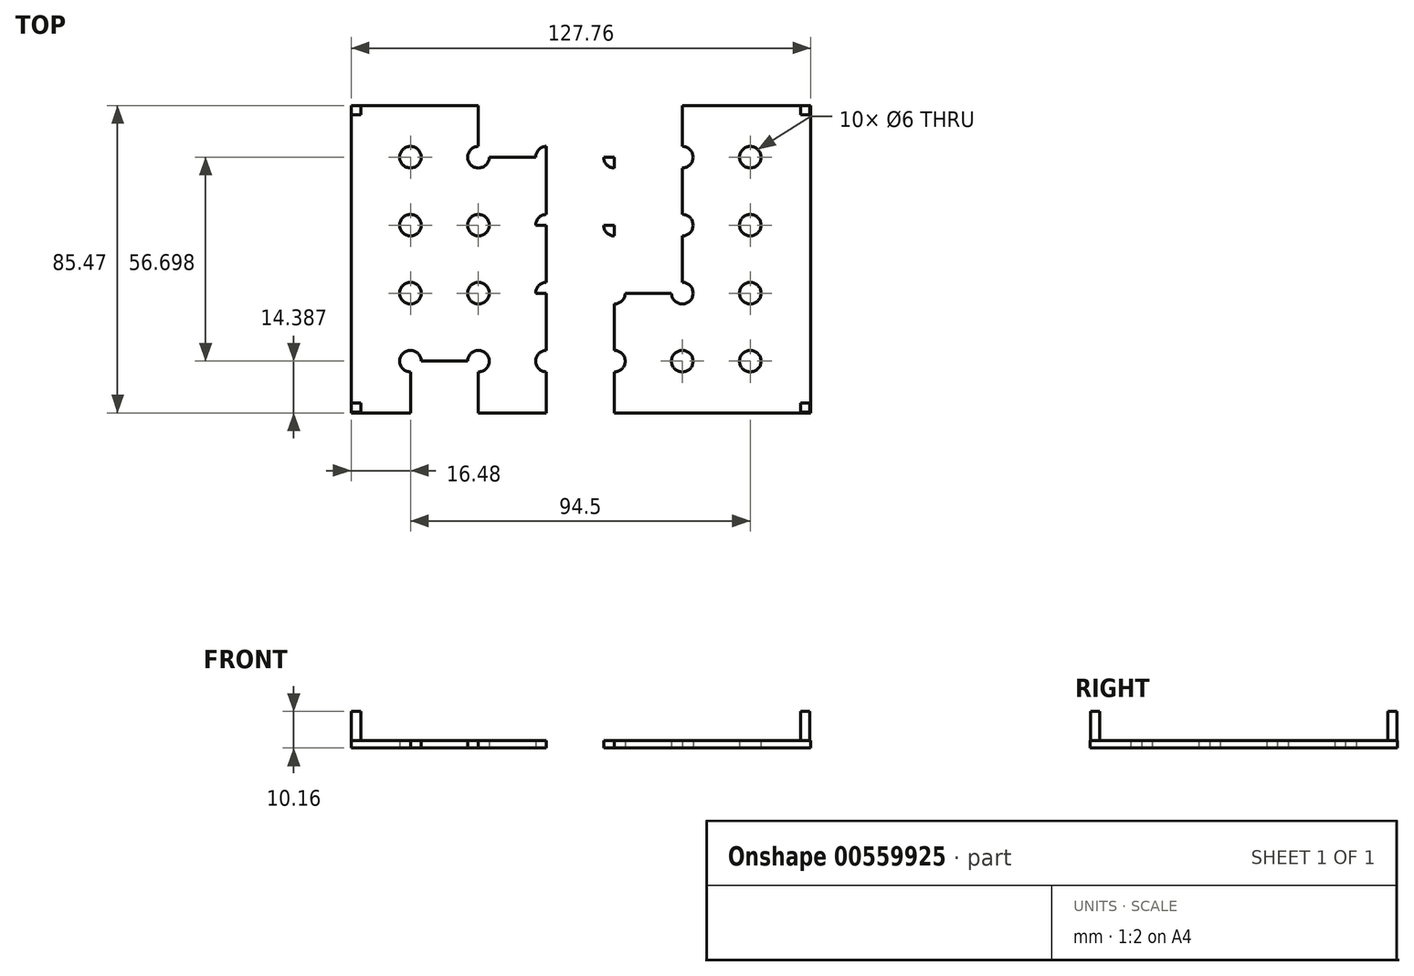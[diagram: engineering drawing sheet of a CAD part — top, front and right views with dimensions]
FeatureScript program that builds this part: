
annotation { "Feature Type Name" : "Feature", "Feature Type Description" : "" }
export const myFeature = defineFeature(function(context is Context, id is Id, definition is map)
    precondition{}
    {
        {
            var Q0;
            Q0=qCreatedBy(makeId("Top.planeOp"),FACE);
            var sketch = newSketch(context, id + "F0", { "sketchPlane" : qUnion([Q0])});
            skLineSegment(sketch, "E0.bottom", {"start": v(63.88, 42.74) * mm, "end": v(-63.88, 42.74) * mm});
            skLineSegment(sketch, "E0.top", {"start": v(63.88, -42.73) * mm, "end": v(-63.88, -42.73) * mm});
            skLineSegment(sketch, "E0.left", {"start": v(63.88, 42.74) * mm, "end": v(63.88, -42.73) * mm});
            skLineSegment(sketch, "E0.right", {"start": v(-63.88, 42.74) * mm, "end": v(-63.88, -42.73) * mm});
            skPoint(sketch, "E0.middle", {"position": v(0, 0) * mm});
            skLineSegment(sketch, "E1", {"start": v(-63.88, 28.34) * mm, "end": v(63.88, 28.35) * mm});
            skLineSegment(sketch, "E2", {"start": v(-63.88, 9.44) * mm, "end": v(63.88, 9.45) * mm});
            skLineSegment(sketch, "E3", {"start": v(-63.88, -9.45) * mm, "end": v(63.88, -9.45) * mm});
            skLineSegment(sketch, "E4", {"start": v(-47.4, 42.74) * mm, "end": v(-47.4, -42.73) * mm});
            skLineSegment(sketch, "E5", {"start": v(-47.4, -42.74) * mm, "end": v(-28.5, -42.73) * mm});
            skLineSegment(sketch, "E6", {"start": v(-28.5, -42.73) * mm, "end": v(-28.5, 42.74) * mm});
            skLineSegment(sketch, "E7", {"start": v(-28.5, 42.74) * mm, "end": v(-9.6, 42.74) * mm});
            skLineSegment(sketch, "E8", {"start": v(-9.6, 42.74) * mm, "end": v(-9.6, -42.73) * mm});
            skLineSegment(sketch, "E9", {"start": v(-9.6, -42.74) * mm, "end": v(9.3, -42.73) * mm});
            skLineSegment(sketch, "E10", {"start": v(9.3, -42.73) * mm, "end": v(9.3, 42.74) * mm});
            skLineSegment(sketch, "E11", {"start": v(9.3, 42.74) * mm, "end": v(28.2, 42.74) * mm});
            skLineSegment(sketch, "E12", {"start": v(28.2, 42.74) * mm, "end": v(28.2, -42.73) * mm});
            skLineSegment(sketch, "E13", {"start": v(47.1, 42.74) * mm, "end": v(47.1, -42.73) * mm});
            skLineSegment(sketch, "E14", {"start": v(-63.88, -28.35) * mm, "end": v(63.88, -28.35) * mm});
            skCircle(sketch, "E15", {"center": v(-47.4, 28.34) * mm, "radius": 3 * mm});
            skCircle(sketch, "E16", {"center": v(-47.4, 9.45) * mm, "radius": 3 * mm});
            skCircle(sketch, "E17", {"center": v(-47.4, -9.46) * mm, "radius": 3 * mm});
            skCircle(sketch, "E18", {"center": v(-47.4, -28.35) * mm, "radius": 3 * mm});
            skCircle(sketch, "E19", {"center": v(-28.5, 28.34) * mm, "radius": 3 * mm});
            skCircle(sketch, "E20", {"center": v(-28.5, 9.45) * mm, "radius": 3 * mm});
            skCircle(sketch, "E21", {"center": v(-28.5, -9.46) * mm, "radius": 3 * mm});
            skCircle(sketch, "E22", {"center": v(-28.5, -28.35) * mm, "radius": 3 * mm});
            skCircle(sketch, "E23", {"center": v(-9.6, 28.34) * mm, "radius": 3 * mm});
            skCircle(sketch, "E24", {"center": v(-9.6, 9.45) * mm, "radius": 3 * mm});
            skCircle(sketch, "E25", {"center": v(-9.6, -9.46) * mm, "radius": 3 * mm});
            skCircle(sketch, "E26", {"center": v(-9.6, -28.35) * mm, "radius": 3 * mm});
            skCircle(sketch, "E27", {"center": v(9.3, 28.34) * mm, "radius": 3 * mm});
            skCircle(sketch, "E28", {"center": v(9.3, 9.45) * mm, "radius": 3 * mm});
            skCircle(sketch, "E29", {"center": v(9.3, -9.46) * mm, "radius": 3 * mm});
            skCircle(sketch, "E30", {"center": v(9.3, -28.35) * mm, "radius": 3 * mm});
            skCircle(sketch, "E31", {"center": v(28.2, 28.34) * mm, "radius": 3 * mm});
            skCircle(sketch, "E32", {"center": v(28.2, 9.45) * mm, "radius": 3 * mm});
            skCircle(sketch, "E33", {"center": v(28.2, -9.46) * mm, "radius": 3 * mm});
            skCircle(sketch, "E34", {"center": v(28.2, -28.35) * mm, "radius": 3 * mm});
            skCircle(sketch, "E35", {"center": v(47.1, 28.34) * mm, "radius": 3 * mm});
            skCircle(sketch, "E36", {"center": v(47.1, 9.45) * mm, "radius": 3 * mm});
            skCircle(sketch, "E37", {"center": v(47.1, -9.46) * mm, "radius": 3 * mm});
            skCircle(sketch, "E38", {"center": v(47.1, -28.35) * mm, "radius": 3 * mm});
            skSolve(sketch);
        }
        {
            var Q0;
            {var subQ1=sQuery(id+"F0.wireOp",EDGE,"E0.bottom");var subQ6=sQuery(id+"F0.wireOp",EDGE,"E0.right");var subQ9=makeQuery(id+"F0.imprint","INTERSECT",VERTEX,{"derivedFrom":[subQ1,subQ6]});Q0=makeQuery(id+"F0.imprint","IMPRINT",FACE,{"disambiguationData":[TD([[makeQuery(id+"F0.imprint","IMPRINT",EDGE,{"disambiguationData":[TD([[subQ9,1.0]])],"derivedFrom":subQ1}),1.0]])]});}
            var Q1;
            {var subQ3=sQuery(id+"F0.wireOp",EDGE,"E15");var subQ9=sQuery(id+"F0.wireOp",EDGE,"E1");var subQ10=makeQuery(id+"F0.imprint","INTERSECT",VERTEX,{"disambiguationData":[OD(1.0)],"derivedFrom":[subQ9,subQ3]});Q1=makeQuery(id+"F0.imprint","IMPRINT",FACE,{"disambiguationData":[TD([[makeQuery(id+"F0.imprint","IMPRINT",EDGE,{"disambiguationData":[TD([[subQ10,-1.0]])],"derivedFrom":subQ9}),1.0]])]});}
            var Q2;
            {var subQ1=sQuery(id+"F0.wireOp",EDGE,"E0.right");var subQ9=sQuery(id+"F0.wireOp",EDGE,"E1");var subQ10=makeQuery(id+"F0.imprint","INTERSECT",VERTEX,{"derivedFrom":[subQ1,subQ9]});Q2=makeQuery(id+"F0.imprint","IMPRINT",FACE,{"disambiguationData":[TD([[makeQuery(id+"F0.imprint","IMPRINT",EDGE,{"disambiguationData":[TD([[subQ10,-1.0]])],"derivedFrom":subQ1}),1.0]])]});}
            var Q3;
            {var subQ5=sQuery(id+"F0.wireOp",EDGE,"E15");var subQ6=sQuery(id+"F0.wireOp",EDGE,"E1");var subQ7=makeQuery(id+"F0.imprint","INTERSECT",VERTEX,{"disambiguationData":[OD(1.0)],"derivedFrom":[subQ6,subQ5]});Q3=makeQuery(id+"F0.imprint","IMPRINT",FACE,{"disambiguationData":[TD([[makeQuery(id+"F0.imprint","IMPRINT",EDGE,{"disambiguationData":[TD([[subQ7,-1.0]])],"derivedFrom":subQ6}),-1.0]])]});}
            var Q4;
            {var subQ8=sQuery(id+"F0.wireOp",EDGE,"E19");var subQ13=sQuery(id+"F0.wireOp",EDGE,"E1");var subQ14=makeQuery(id+"F0.imprint","INTERSECT",VERTEX,{"disambiguationData":[OD(1.0)],"derivedFrom":[subQ13,subQ8]});Q4=makeQuery(id+"F0.imprint","IMPRINT",FACE,{"disambiguationData":[TD([[makeQuery(id+"F0.imprint","IMPRINT",EDGE,{"disambiguationData":[TD([[subQ14,-1.0]])],"derivedFrom":subQ13}),-1.0]])]});}
            var Q5;
            {var subQ1=sQuery(id+"F0.wireOp",EDGE,"E7");Q5=makeQuery(id+"F0.imprint","IMPRINT",FACE,{"disambiguationData":[TD([[makeQuery(id+"F0.imprint","IMPRINT",EDGE,{"derivedFrom":subQ1}),-1.0]])]});}
            var Q6;
            {var subQ5=sQuery(id+"F0.wireOp",EDGE,"E23");var subQ6=sQuery(id+"F0.wireOp",EDGE,"E1");var subQ7=makeQuery(id+"F0.imprint","INTERSECT",VERTEX,{"disambiguationData":[OD(1.0)],"derivedFrom":[subQ6,subQ5]});Q6=makeQuery(id+"F0.imprint","IMPRINT",FACE,{"disambiguationData":[TD([[makeQuery(id+"F0.imprint","IMPRINT",EDGE,{"disambiguationData":[TD([[subQ7,-1.0]])],"derivedFrom":subQ6}),-1.0]])]});}
            var Q7;
            {var subQ7=sQuery(id+"F0.wireOp",EDGE,"E23");var subQ9=sQuery(id+"F0.wireOp",EDGE,"E1");var subQ10=makeQuery(id+"F0.imprint","INTERSECT",VERTEX,{"disambiguationData":[OD(1.0)],"derivedFrom":[subQ9,subQ7]});Q7=makeQuery(id+"F0.imprint","IMPRINT",FACE,{"disambiguationData":[TD([[makeQuery(id+"F0.imprint","IMPRINT",EDGE,{"disambiguationData":[TD([[subQ10,-1.0]])],"derivedFrom":subQ9}),1.0]])]});}
            var Q8;
            {var subQ1=sQuery(id+"F0.wireOp",EDGE,"E11");Q8=makeQuery(id+"F0.imprint","IMPRINT",FACE,{"disambiguationData":[TD([[makeQuery(id+"F0.imprint","IMPRINT",EDGE,{"derivedFrom":subQ1}),-1.0]])]});}
            var Q9;
            {var subQ3=sQuery(id+"F0.wireOp",EDGE,"E27");var subQ13=sQuery(id+"F0.wireOp",EDGE,"E1");var subQ14=makeQuery(id+"F0.imprint","INTERSECT",VERTEX,{"disambiguationData":[OD(1.0)],"derivedFrom":[subQ13,subQ3]});Q9=makeQuery(id+"F0.imprint","IMPRINT",FACE,{"disambiguationData":[TD([[makeQuery(id+"F0.imprint","IMPRINT",EDGE,{"disambiguationData":[TD([[subQ14,-1.0]])],"derivedFrom":subQ13}),-1.0]])]});}
            var Q10;
            {var subQ0=sQuery(id+"F0.wireOp",EDGE,"E31");var subQ13=sQuery(id+"F0.wireOp",EDGE,"E1");var subQ14=makeQuery(id+"F0.imprint","INTERSECT",VERTEX,{"disambiguationData":[OD(1.0)],"derivedFrom":[subQ13,subQ0]});Q10=makeQuery(id+"F0.imprint","IMPRINT",FACE,{"disambiguationData":[TD([[makeQuery(id+"F0.imprint","IMPRINT",EDGE,{"disambiguationData":[TD([[subQ14,-1.0]])],"derivedFrom":subQ13}),-1.0]])]});}
            var Q11;
            {var subQ3=sQuery(id+"F0.wireOp",EDGE,"E31");var subQ7=sQuery(id+"F0.wireOp",EDGE,"E1");var subQ8=makeQuery(id+"F0.imprint","INTERSECT",VERTEX,{"disambiguationData":[OD(1.0)],"derivedFrom":[subQ7,subQ3]});Q11=makeQuery(id+"F0.imprint","IMPRINT",FACE,{"disambiguationData":[TD([[makeQuery(id+"F0.imprint","IMPRINT",EDGE,{"disambiguationData":[TD([[subQ8,-1.0]])],"derivedFrom":subQ7}),1.0]])]});}
            var Q12;
            {var subQ1=sQuery(id+"F0.wireOp",EDGE,"E0.bottom");var subQ6=sQuery(id+"F0.wireOp",EDGE,"E0.left");var subQ9=makeQuery(id+"F0.imprint","INTERSECT",VERTEX,{"derivedFrom":[subQ1,subQ6]});Q12=makeQuery(id+"F0.imprint","IMPRINT",FACE,{"disambiguationData":[TD([[makeQuery(id+"F0.imprint","IMPRINT",EDGE,{"disambiguationData":[TD([[subQ9,-1.0]])],"derivedFrom":subQ1}),1.0]])]});}
            var Q13;
            {var subQ6=sQuery(id+"F0.wireOp",EDGE,"E0.left");var subQ9=sQuery(id+"F0.wireOp",EDGE,"E1");var subQ10=makeQuery(id+"F0.imprint","INTERSECT",VERTEX,{"derivedFrom":[subQ6,subQ9]});Q13=makeQuery(id+"F0.imprint","IMPRINT",FACE,{"disambiguationData":[TD([[makeQuery(id+"F0.imprint","IMPRINT",EDGE,{"disambiguationData":[TD([[subQ10,-1.0]])],"derivedFrom":subQ6}),-1.0]])]});}
            var Q14;
            {var subQ1=sQuery(id+"F0.wireOp",EDGE,"E0.left");var subQ9=sQuery(id+"F0.wireOp",EDGE,"E2");var subQ10=makeQuery(id+"F0.imprint","INTERSECT",VERTEX,{"derivedFrom":[subQ1,subQ9]});Q14=makeQuery(id+"F0.imprint","IMPRINT",FACE,{"disambiguationData":[TD([[makeQuery(id+"F0.imprint","IMPRINT",EDGE,{"disambiguationData":[TD([[subQ10,-1.0]])],"derivedFrom":subQ1}),-1.0]])]});}
            var Q15;
            {var subQ9=sQuery(id+"F0.wireOp",EDGE,"E32");var subQ13=sQuery(id+"F0.wireOp",EDGE,"E2");var subQ14=makeQuery(id+"F0.imprint","INTERSECT",VERTEX,{"disambiguationData":[OD(1.0)],"derivedFrom":[subQ13,subQ9]});Q15=makeQuery(id+"F0.imprint","IMPRINT",FACE,{"disambiguationData":[TD([[makeQuery(id+"F0.imprint","IMPRINT",EDGE,{"disambiguationData":[TD([[subQ14,-1.0]])],"derivedFrom":subQ13}),-1.0]])]});}
            var Q16;
            {var subQ5=sQuery(id+"F0.wireOp",EDGE,"E28");var subQ6=sQuery(id+"F0.wireOp",EDGE,"E2");var subQ7=makeQuery(id+"F0.imprint","INTERSECT",VERTEX,{"disambiguationData":[OD(1.0)],"derivedFrom":[subQ6,subQ5]});Q16=makeQuery(id+"F0.imprint","IMPRINT",FACE,{"disambiguationData":[TD([[makeQuery(id+"F0.imprint","IMPRINT",EDGE,{"disambiguationData":[TD([[subQ7,-1.0]])],"derivedFrom":subQ6}),-1.0]])]});}
            var Q17;
            {var subQ5=sQuery(id+"F0.wireOp",EDGE,"E24");var subQ6=sQuery(id+"F0.wireOp",EDGE,"E2");var subQ7=makeQuery(id+"F0.imprint","INTERSECT",VERTEX,{"disambiguationData":[OD(1.0)],"derivedFrom":[subQ6,subQ5]});Q17=makeQuery(id+"F0.imprint","IMPRINT",FACE,{"disambiguationData":[TD([[makeQuery(id+"F0.imprint","IMPRINT",EDGE,{"disambiguationData":[TD([[subQ7,-1.0]])],"derivedFrom":subQ6}),-1.0]])]});}
            var Q18;
            {var subQ5=sQuery(id+"F0.wireOp",EDGE,"E20");var subQ6=sQuery(id+"F0.wireOp",EDGE,"E2");var subQ7=makeQuery(id+"F0.imprint","INTERSECT",VERTEX,{"disambiguationData":[OD(1.0)],"derivedFrom":[subQ6,subQ5]});Q18=makeQuery(id+"F0.imprint","IMPRINT",FACE,{"disambiguationData":[TD([[makeQuery(id+"F0.imprint","IMPRINT",EDGE,{"disambiguationData":[TD([[subQ7,-1.0]])],"derivedFrom":subQ6}),-1.0]])]});}
            var Q19;
            {var subQ0=sQuery(id+"F0.wireOp",EDGE,"E16");var subQ13=sQuery(id+"F0.wireOp",EDGE,"E2");var subQ14=makeQuery(id+"F0.imprint","INTERSECT",VERTEX,{"disambiguationData":[OD(1.0)],"derivedFrom":[subQ13,subQ0]});Q19=makeQuery(id+"F0.imprint","IMPRINT",FACE,{"disambiguationData":[TD([[makeQuery(id+"F0.imprint","IMPRINT",EDGE,{"disambiguationData":[TD([[subQ14,-1.0]])],"derivedFrom":subQ13}),-1.0]])]});}
            var Q20;
            {var subQ5=sQuery(id+"F0.wireOp",EDGE,"E2");var subQ6=sQuery(id+"F0.wireOp",EDGE,"E0.right");var subQ7=makeQuery(id+"F0.imprint","INTERSECT",VERTEX,{"derivedFrom":[subQ6,subQ5]});Q20=makeQuery(id+"F0.imprint","IMPRINT",FACE,{"disambiguationData":[TD([[makeQuery(id+"F0.imprint","IMPRINT",EDGE,{"disambiguationData":[TD([[subQ7,-1.0]])],"derivedFrom":subQ6}),1.0]])]});}
            var Q21;
            {var subQ1=sQuery(id+"F0.wireOp",EDGE,"E0.right");var subQ9=sQuery(id+"F0.wireOp",EDGE,"E3");var subQ10=makeQuery(id+"F0.imprint","INTERSECT",VERTEX,{"derivedFrom":[subQ1,subQ9]});Q21=makeQuery(id+"F0.imprint","IMPRINT",FACE,{"disambiguationData":[TD([[makeQuery(id+"F0.imprint","IMPRINT",EDGE,{"disambiguationData":[TD([[subQ10,-1.0]])],"derivedFrom":subQ1}),1.0]])]});}
            var Q22;
            {var subQ9=sQuery(id+"F0.wireOp",EDGE,"E17");var subQ10=sQuery(id+"F0.wireOp",EDGE,"E3");var subQ11=makeQuery(id+"F0.imprint","INTERSECT",VERTEX,{"disambiguationData":[OD(1.0)],"derivedFrom":[subQ10,subQ9]});Q22=makeQuery(id+"F0.imprint","IMPRINT",FACE,{"disambiguationData":[TD([[makeQuery(id+"F0.imprint","IMPRINT",EDGE,{"disambiguationData":[TD([[subQ11,-1.0]])],"derivedFrom":subQ10}),-1.0]])]});}
            var Q23;
            {var subQ6=sQuery(id+"F0.wireOp",EDGE,"E3");var subQ13=sQuery(id+"F0.wireOp",EDGE,"E21");var subQ15=makeQuery(id+"F0.imprint","INTERSECT",VERTEX,{"disambiguationData":[OD(1.0)],"derivedFrom":[subQ6,subQ13]});Q23=makeQuery(id+"F0.imprint","IMPRINT",FACE,{"disambiguationData":[TD([[makeQuery(id+"F0.imprint","IMPRINT",EDGE,{"disambiguationData":[TD([[subQ15,-1.0]])],"derivedFrom":subQ6}),-1.0]])]});}
            var Q24;
            {var subQ5=sQuery(id+"F0.wireOp",EDGE,"E25");var subQ13=sQuery(id+"F0.wireOp",EDGE,"E3");var subQ14=makeQuery(id+"F0.imprint","INTERSECT",VERTEX,{"disambiguationData":[OD(1.0)],"derivedFrom":[subQ13,subQ5]});Q24=makeQuery(id+"F0.imprint","IMPRINT",FACE,{"disambiguationData":[TD([[makeQuery(id+"F0.imprint","IMPRINT",EDGE,{"disambiguationData":[TD([[subQ14,-1.0]])],"derivedFrom":subQ13}),-1.0]])]});}
            var Q25;
            {var subQ5=sQuery(id+"F0.wireOp",EDGE,"E29");var subQ6=sQuery(id+"F0.wireOp",EDGE,"E3");var subQ7=makeQuery(id+"F0.imprint","INTERSECT",VERTEX,{"disambiguationData":[OD(1.0)],"derivedFrom":[subQ6,subQ5]});Q25=makeQuery(id+"F0.imprint","IMPRINT",FACE,{"disambiguationData":[TD([[makeQuery(id+"F0.imprint","IMPRINT",EDGE,{"disambiguationData":[TD([[subQ7,-1.0]])],"derivedFrom":subQ6}),-1.0]])]});}
            var Q26;
            {var subQ11=sQuery(id+"F0.wireOp",EDGE,"E33");var subQ13=sQuery(id+"F0.wireOp",EDGE,"E3");var subQ14=makeQuery(id+"F0.imprint","INTERSECT",VERTEX,{"disambiguationData":[OD(1.0)],"derivedFrom":[subQ13,subQ11]});Q26=makeQuery(id+"F0.imprint","IMPRINT",FACE,{"disambiguationData":[TD([[makeQuery(id+"F0.imprint","IMPRINT",EDGE,{"disambiguationData":[TD([[subQ14,-1.0]])],"derivedFrom":subQ13}),-1.0]])]});}
            var Q27;
            {var subQ1=sQuery(id+"F0.wireOp",EDGE,"E0.left");var subQ9=sQuery(id+"F0.wireOp",EDGE,"E3");var subQ10=makeQuery(id+"F0.imprint","INTERSECT",VERTEX,{"derivedFrom":[subQ1,subQ9]});Q27=makeQuery(id+"F0.imprint","IMPRINT",FACE,{"disambiguationData":[TD([[makeQuery(id+"F0.imprint","IMPRINT",EDGE,{"disambiguationData":[TD([[subQ10,-1.0]])],"derivedFrom":subQ1}),-1.0]])]});}
            var Q28;
            {var subQ1=sQuery(id+"F0.wireOp",EDGE,"E0.left");var subQ6=sQuery(id+"F0.wireOp",EDGE,"E0.top");var subQ9=makeQuery(id+"F0.imprint","INTERSECT",VERTEX,{"derivedFrom":[subQ6,subQ1]});Q28=makeQuery(id+"F0.imprint","IMPRINT",FACE,{"disambiguationData":[TD([[makeQuery(id+"F0.imprint","IMPRINT",EDGE,{"disambiguationData":[TD([[subQ9,-1.0]])],"derivedFrom":subQ6}),-1.0]])]});}
            var Q29;
            {var subQ6=sQuery(id+"F0.wireOp",EDGE,"E0.top");var subQ9=sQuery(id+"F0.wireOp",EDGE,"E12");var subQ11=makeQuery(id+"F0.imprint","INTERSECT",VERTEX,{"derivedFrom":[subQ6,subQ9]});Q29=makeQuery(id+"F0.imprint","IMPRINT",FACE,{"disambiguationData":[TD([[makeQuery(id+"F0.imprint","IMPRINT",EDGE,{"disambiguationData":[TD([[subQ11,1.0]])],"derivedFrom":subQ6}),-1.0]])]});}
            var Q30;
            {var subQ5=sQuery(id+"F0.wireOp",EDGE,"E12");var subQ6=sQuery(id+"F0.wireOp",EDGE,"E0.top");var subQ7=makeQuery(id+"F0.imprint","INTERSECT",VERTEX,{"derivedFrom":[subQ6,subQ5]});Q30=makeQuery(id+"F0.imprint","IMPRINT",FACE,{"disambiguationData":[TD([[makeQuery(id+"F0.imprint","IMPRINT",EDGE,{"disambiguationData":[TD([[subQ7,1.0]])],"derivedFrom":subQ5}),-1.0]])]});}
            var Q31;
            {var subQ1=sQuery(id+"F0.wireOp",EDGE,"E9");Q31=makeQuery(id+"F0.imprint","IMPRINT",FACE,{"disambiguationData":[TD([[makeQuery(id+"F0.imprint","IMPRINT",EDGE,{"derivedFrom":subQ1}),1.0]])]});}
            var Q32;
            {var subQ6=sQuery(id+"F0.wireOp",EDGE,"E5");Q32=makeQuery(id+"F0.imprint","IMPRINT",FACE,{"disambiguationData":[TD([[makeQuery(id+"F0.imprint","IMPRINT",EDGE,{"derivedFrom":subQ6}),1.0]])]});}
            var Q33;
            {var subQ0=sQuery(id+"F0.wireOp",EDGE,"E22");var subQ1=sQuery(id+"F0.wireOp",EDGE,"E14");var subQ2=makeQuery(id+"F0.imprint","INTERSECT",VERTEX,{"disambiguationData":[OD(1.0)],"derivedFrom":[subQ1,subQ0]});Q33=makeQuery(id+"F0.imprint","IMPRINT",FACE,{"disambiguationData":[TD([[makeQuery(id+"F0.imprint","IMPRINT",EDGE,{"disambiguationData":[TD([[subQ2,-1.0]])],"derivedFrom":subQ1}),-1.0]])]});}
            var Q34;
            {var subQ1=sQuery(id+"F0.wireOp",EDGE,"E0.right");var subQ6=sQuery(id+"F0.wireOp",EDGE,"E0.top");var subQ9=makeQuery(id+"F0.imprint","INTERSECT",VERTEX,{"derivedFrom":[subQ6,subQ1]});Q34=makeQuery(id+"F0.imprint","IMPRINT",FACE,{"disambiguationData":[TD([[makeQuery(id+"F0.imprint","IMPRINT",EDGE,{"disambiguationData":[TD([[subQ9,1.0]])],"derivedFrom":subQ1}),1.0]])]});}
            extrude(context, id + "F1", {"entities" : qUnion([Q0, Q1, Q2, Q3, Q4, Q5, Q6, Q7, Q8, Q9, Q10, Q11, Q12, Q13, Q14, Q15, Q16, Q17, Q18, Q19, Q20, Q21, Q22, Q23, Q24, Q25, Q26, Q27, Q28, Q29, Q30, Q31, Q32, Q33, Q34]), "depth" : 2 * mm, "offsetDistance" : 25.4 * mm});
        }
        {
            var Q0;
            Q0=qCreatedBy(makeId("Top.planeOp"),FACE);
            var sketch = newSketch(context, id + "F2", { "sketchPlane" : qUnion([Q0])});
            skPoint(sketch, "E39", {"position": v(-63.8, 42.68) * mm});
            skLineSegment(sketch, "E40.bottom", {"start": v(-63.8, 42.68) * mm, "end": v(-61.26, 42.68) * mm});
            skLineSegment(sketch, "E40.top", {"start": v(-63.8, 40.14) * mm, "end": v(-61.26, 40.14) * mm});
            skLineSegment(sketch, "E40.left", {"start": v(-63.8, 42.68) * mm, "end": v(-63.8, 40.14) * mm});
            skLineSegment(sketch, "E40.right", {"start": v(-61.26, 42.68) * mm, "end": v(-61.26, 40.14) * mm});
            skLineSegment(sketch, "E41.bottom", {"start": v(-63.8, -40.06) * mm, "end": v(-61.26, -40.06) * mm});
            skLineSegment(sketch, "E41.top", {"start": v(-63.8, -42.6) * mm, "end": v(-61.26, -42.6) * mm});
            skLineSegment(sketch, "E41.left", {"start": v(-63.8, -40.06) * mm, "end": v(-63.8, -42.6) * mm});
            skLineSegment(sketch, "E41.right", {"start": v(-61.26, -40.06) * mm, "end": v(-61.26, -42.6) * mm});
            skLineSegment(sketch, "E42.bottom", {"start": v(61.09, -40.06) * mm, "end": v(63.63, -40.06) * mm});
            skLineSegment(sketch, "E42.top", {"start": v(61.09, -42.6) * mm, "end": v(63.63, -42.6) * mm});
            skLineSegment(sketch, "E42.left", {"start": v(61.09, -40.06) * mm, "end": v(61.09, -42.6) * mm});
            skLineSegment(sketch, "E42.right", {"start": v(63.63, -40.06) * mm, "end": v(63.63, -42.6) * mm});
            skLineSegment(sketch, "E43.bottom", {"start": v(61.09, 42.68) * mm, "end": v(63.63, 42.68) * mm});
            skLineSegment(sketch, "E43.top", {"start": v(61.09, 40.14) * mm, "end": v(63.63, 40.14) * mm});
            skLineSegment(sketch, "E43.left", {"start": v(61.09, 42.68) * mm, "end": v(61.09, 40.14) * mm});
            skLineSegment(sketch, "E43.right", {"start": v(63.63, 42.68) * mm, "end": v(63.63, 40.14) * mm});
            skSolve(sketch);
        }
        {
            var Q0;
            Q0 = qSketchRegion(id + "F2", true);
            extrude(context, id + "F3", {"entities" : qUnion([Q0]), "operationType" : NewBodyOperationType.ADD, "depth" : 10.16 * mm, "offsetDistance" : 25.4 * mm});
        }
    });
